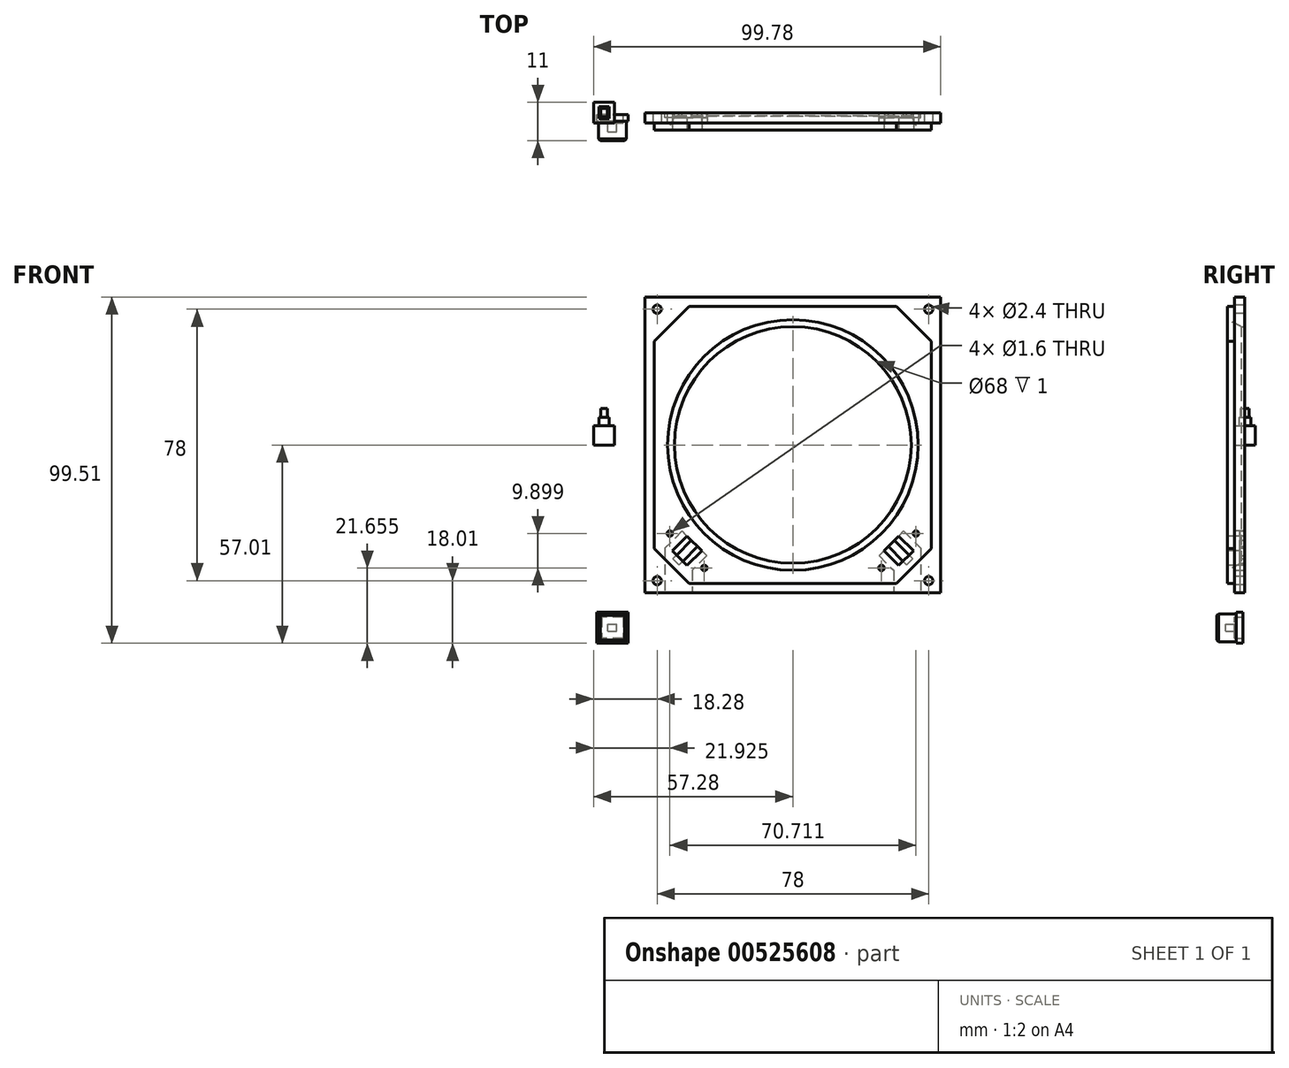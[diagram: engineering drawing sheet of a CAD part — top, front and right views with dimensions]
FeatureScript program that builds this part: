
annotation { "Feature Type Name" : "Feature", "Feature Type Description" : "" }
export const myFeature = defineFeature(function(context is Context, id is Id, definition is map)
    precondition{}
    {
        {
            var Q0;
            Q0=qCreatedBy(makeId("Front.planeOp"),FACE);
            cPlane(context, id + "F0", {"entities" : qUnion([Q0]), "cplaneType" : CPlaneType.OFFSET, "offset" : 3 * mm, "width" : 150 * mm, "height" : 150 * mm});
        }
        {
            var Q0;
            Q0=qCreatedBy(id+"F0.planeOp",FACE);
            var sketch = newSketch(context, id + "F1", { "sketchPlane" : qUnion([Q0])});
            skLineSegment(sketch, "E0.0", {"start": v(39.8, 29.8) * mm, "end": v(39.8, 0) * mm});
            skLineSegment(sketch, "E0.1", {"start": v(39.8, -29.8) * mm, "end": v(29.8, -39.8) * mm});
            skLineSegment(sketch, "E0.2", {"start": v(29.8, -39.8) * mm, "end": v(0, -39.8) * mm});
            skLineSegment(sketch, "E0.3", {"start": v(-29.8, -39.8) * mm, "end": v(-39.8, -29.8) * mm});
            skLineSegment(sketch, "E0.4", {"start": v(-39.8, -29.8) * mm, "end": v(-39.8, 0) * mm});
            skLineSegment(sketch, "E0.5", {"start": v(-39.8, 29.8) * mm, "end": v(-29.8, 39.8) * mm});
            skLineSegment(sketch, "E0.6", {"start": v(-29.8, 39.8) * mm, "end": v(0, 39.8) * mm});
            skLineSegment(sketch, "E0.7", {"start": v(29.8, 39.8) * mm, "end": v(39.8, 29.8) * mm});
            skPoint(sketch, "E1", {"position": v(0, 0) * mm});
            skLineSegment(sketch, "E2", {"start": v(0, 39.8) * mm, "end": v(29.8, 39.8) * mm});
            skLineSegment(sketch, "E3", {"start": v(-39.8, 0) * mm, "end": v(-39.8, 29.8) * mm});
            skLineSegment(sketch, "E4", {"start": v(39.8, 0) * mm, "end": v(39.8, -29.8) * mm});
            skLineSegment(sketch, "E5", {"start": v(0, -39.8) * mm, "end": v(-29.8, -39.8) * mm});
            skSolve(sketch);
        }
        {
            var Q0;
            Q0=qSketchRegion(id+"F1",true);
            extrude(context, id + "F2", {"entities" : qUnion([Q0]), "depth" : 2 * mm});
        }
        {
            var Q0;
            Q0=makeQuery(id+"F2.opExtrude","CAP_FACE",FACE,{"disambiguationData":[OSD([sQuery(id+"F1.wireOp",EDGE,"E0.0"),sQuery(id+"F1.wireOp",EDGE,"E0.1"),sQuery(id+"F1.wireOp",EDGE,"E0.2"),sQuery(id+"F1.wireOp",EDGE,"E0.3"),sQuery(id+"F1.wireOp",EDGE,"E0.4"),sQuery(id+"F1.wireOp",EDGE,"E0.5"),sQuery(id+"F1.wireOp",EDGE,"E0.6"),sQuery(id+"F1.wireOp",EDGE,"E0.7"),sQuery(id+"F1.wireOp",EDGE,"E2"),sQuery(id+"F1.wireOp",EDGE,"E3"),sQuery(id+"F1.wireOp",EDGE,"E4"),sQuery(id+"F1.wireOp",EDGE,"E5")])],"isStart":true});
            var sketch = newSketch(context, id + "F3", { "sketchPlane" : qUnion([Q0])});
            skLineSegment(sketch, "E6.bottom", {"start": v(-42.5, -42.5) * mm, "end": v(42.5, -42.5) * mm});
            skLineSegment(sketch, "E6.top", {"start": v(-42.5, 42.5) * mm, "end": v(42.5, 42.5) * mm});
            skLineSegment(sketch, "E6.left", {"start": v(-42.5, -42.5) * mm, "end": v(-42.5, 42.5) * mm});
            skLineSegment(sketch, "E6.right", {"start": v(42.5, -42.5) * mm, "end": v(42.5, 42.5) * mm});
            skPoint(sketch, "E6.middle", {"position": v(0, 0) * mm});
            skSolve(sketch);
        }
        {
            var Q0;
            Q0=qSketchRegion(id+"F3",true);
            extrude(context, id + "F4", {"entities" : qUnion([Q0]), "operationType" : NewBodyOperationType.ADD, "depth" : 3 * mm, "offsetDistance" : 25 * mm});
        }
        {
            var Q0;
            Q0=makeQuery(id+"F2.opExtrude","CAP_FACE",FACE,{"disambiguationData":[OSD([sQuery(id+"F1.wireOp",EDGE,"E0.0"),sQuery(id+"F1.wireOp",EDGE,"E0.1"),sQuery(id+"F1.wireOp",EDGE,"E0.2"),sQuery(id+"F1.wireOp",EDGE,"E0.3"),sQuery(id+"F1.wireOp",EDGE,"E0.4"),sQuery(id+"F1.wireOp",EDGE,"E0.5"),sQuery(id+"F1.wireOp",EDGE,"E0.6"),sQuery(id+"F1.wireOp",EDGE,"E0.7"),sQuery(id+"F1.wireOp",EDGE,"E2"),sQuery(id+"F1.wireOp",EDGE,"E3"),sQuery(id+"F1.wireOp",EDGE,"E4"),sQuery(id+"F1.wireOp",EDGE,"E5")])],"isStart":false});
            var sketch = newSketch(context, id + "F5", { "sketchPlane" : qUnion([Q0])});
            skCircle(sketch, "E7", {"center": v(0, 0) * mm, "radius": 38 * mm});
            skCircle(sketch, "E8", {"center": v(-39, 39) * mm, "radius": 1.5 * mm});
            skCircle(sketch, "E9", {"center": v(39, 39) * mm, "radius": 1.5 * mm});
            skCircle(sketch, "E10", {"center": v(-39, -39) * mm, "radius": 1.5 * mm});
            skCircle(sketch, "E11", {"center": v(39, -39) * mm, "radius": 1.5 * mm});
            skSolve(sketch);
        }
        {
            var Q0;
            Q0=sQuery(id+"F5.wireOp",VERTEX,"E8.center");
            var Q1;
            Q1=sQuery(id+"F5.wireOp",VERTEX,"E9.center");
            var Q2;
            Q2=sQuery(id+"F5.wireOp",VERTEX,"E11.center");
            var Q3;
            Q3=sQuery(id+"F5.wireOp",VERTEX,"E10.center");
            var Q4;
            Q4=makeQuery(id+"F2.opExtrude","SWEPT_BODY",BODY,{"disambiguationData":[OSD([sQuery(id+"F1.wireOp",EDGE,"E0.0"),sQuery(id+"F1.wireOp",EDGE,"E0.1"),sQuery(id+"F1.wireOp",EDGE,"E0.2"),sQuery(id+"F1.wireOp",EDGE,"E0.3"),sQuery(id+"F1.wireOp",EDGE,"E0.4"),sQuery(id+"F1.wireOp",EDGE,"E0.5"),sQuery(id+"F1.wireOp",EDGE,"E0.6"),sQuery(id+"F1.wireOp",EDGE,"E0.7"),sQuery(id+"F1.wireOp",EDGE,"E2"),sQuery(id+"F1.wireOp",EDGE,"E3"),sQuery(id+"F1.wireOp",EDGE,"E4"),sQuery(id+"F1.wireOp",EDGE,"E5")])]});
            hole(context, id + "F6", {"style" : HoleStyle.SIMPLE, "endStyle" : HoleEndStyle.THROUGH, "holeDiameter" : 2.4 * mm, "locations" : qUnion([Q0, Q1, Q2, Q3]), "scope" : qUnion([Q4]), "majorDiameter" : 5 * mm, "tappedDepth" : 12 * mm, "tapClearance" : 3});
        }
        {
            var Q0;
            Q0=sQuery(id+"F5.wireOp",VERTEX,"E7.center");
            var Q1;
            Q1=makeQuery(id+"F2.opExtrude","SWEPT_BODY",BODY,{"disambiguationData":[OSD([sQuery(id+"F1.wireOp",EDGE,"E0.0"),sQuery(id+"F1.wireOp",EDGE,"E0.1"),sQuery(id+"F1.wireOp",EDGE,"E0.2"),sQuery(id+"F1.wireOp",EDGE,"E0.3"),sQuery(id+"F1.wireOp",EDGE,"E0.4"),sQuery(id+"F1.wireOp",EDGE,"E0.5"),sQuery(id+"F1.wireOp",EDGE,"E0.6"),sQuery(id+"F1.wireOp",EDGE,"E0.7"),sQuery(id+"F1.wireOp",EDGE,"E2"),sQuery(id+"F1.wireOp",EDGE,"E3"),sQuery(id+"F1.wireOp",EDGE,"E4"),sQuery(id+"F1.wireOp",EDGE,"E5")])]});
            hole(context, id + "F7", {"style" : HoleStyle.SIMPLE, "endStyle" : HoleEndStyle.THROUGH, "holeDiameter" : 76 * mm, "locations" : qUnion([Q0]), "scope" : qUnion([Q1]), "majorDiameter" : 5 * mm, "tappedDepth" : 12 * mm, "tapClearance" : 3});
        }
        {
            var Q0;
            Q0=qCreatedBy(makeId("Right.planeOp"),FACE);
            var sketch = newSketch(context, id + "F8", { "sketchPlane" : qUnion([Q0])});
            skLineSegment(sketch, "E12", {"start": v(-5, 38) * mm, "end": v(-5, 36) * mm});
            skLineSegment(sketch, "E13", {"start": v(0, 34) * mm, "end": v(0, 38) * mm});
            skLineSegment(sketch, "E14", {"start": v(0, 38) * mm, "end": v(-5, 38) * mm});
            skLineSegment(sketch, "E15", {"start": v(0, 34) * mm, "end": v(-1, 34) * mm});
            skLineSegment(sketch, "E16", {"start": v(-1, 34) * mm, "end": v(-5, 36) * mm});
            skLineSegment(sketch, "E17", {"start": v(0, 0) * mm, "end": v(-24.42, 0) * mm, "construction": true});
            skSolve(sketch);
        }
        {
            var Q0;
            Q0 = qSketchRegion(id + "F8", true);
            var Q1;
            Q1=sQuery(id+"F8.wireOp",EDGE,"E17");
            revolve(context, id + "F9", {"operationType" : NewBodyOperationType.ADD, "entities" : qUnion([Q0]), "axis" : qUnion([Q1]), "revolveType" : RevolveType.FULL});
        }
        {
            var Q0;
            Q0=makeQuery(id+"F9.boolean.opBoolean","MERGE",FACE,{"derivedFrom":[makeQuery(id+"F2.opExtrude","CAP_FACE",FACE,{"disambiguationData":[OSD([sQuery(id+"F1.wireOp",EDGE,"E0.0"),sQuery(id+"F1.wireOp",EDGE,"E0.1"),sQuery(id+"F1.wireOp",EDGE,"E0.2"),sQuery(id+"F1.wireOp",EDGE,"E0.3"),sQuery(id+"F1.wireOp",EDGE,"E0.4"),sQuery(id+"F1.wireOp",EDGE,"E0.5"),sQuery(id+"F1.wireOp",EDGE,"E0.6"),sQuery(id+"F1.wireOp",EDGE,"E0.7"),sQuery(id+"F1.wireOp",EDGE,"E2"),sQuery(id+"F1.wireOp",EDGE,"E3"),sQuery(id+"F1.wireOp",EDGE,"E4"),sQuery(id+"F1.wireOp",EDGE,"E5")])],"isStart":false}),makeQuery(id+"F9.opRevolve","SWEPT_FACE",FACE,{"disambiguationData":[OSD([sQuery(id+"F8.wireOp",EDGE,"E12")])]})]});
            var sketch = newSketch(context, id + "F10", { "sketchPlane" : qUnion([Q0])});
            skLineSegment(sketch, "E18.bottom", {"start": v(-26.16, -30.4) * mm, "end": v(-30.4, -34.65) * mm});
            skLineSegment(sketch, "E18.top", {"start": v(-30.4, -26.16) * mm, "end": v(-34.65, -30.4) * mm});
            skLineSegment(sketch, "E18.left", {"start": v(-26.16, -30.4) * mm, "end": v(-30.4, -26.16) * mm});
            skLineSegment(sketch, "E18.right", {"start": v(-30.4, -34.65) * mm, "end": v(-34.65, -30.4) * mm});
            skPoint(sketch, "E18.middle", {"position": v(-30.4, -30.4) * mm});
            skLineSegment(sketch, "E19", {"start": v(0, 0) * mm, "end": v(-49.8, -49.8) * mm, "construction": true});
            skLineSegment(sketch, "E20", {"start": v(0, 0) * mm, "end": v(0, -7.55) * mm, "construction": true});
            skCircle(sketch, "E21", {"center": v(-35.36, -25.46) * mm, "radius": 0.8 * mm});
            skLineSegment(sketch, "E22", {"start": v(-30.4, -24.04) * mm, "end": v(-36.77, -30.4) * mm, "construction": true});
            skLineSegment(sketch, "E23", {"start": v(-36.77, -30.4) * mm, "end": v(-30.4, -36.77) * mm, "construction": true});
            skLineSegment(sketch, "E24", {"start": v(-30.4, -36.77) * mm, "end": v(-24.04, -30.4) * mm, "construction": true});
            skLineSegment(sketch, "E25", {"start": v(-24.04, -30.4) * mm, "end": v(-30.4, -24.04) * mm, "construction": true});
            skCircle(sketch, "E26", {"center": v(-25.46, -35.36) * mm, "radius": 0.8 * mm});
            skLineSegment(sketch, "E27.MirrorCS", {"start": v(0, 0) * mm, "end": v(49.8, -49.8) * mm, "construction": true});
            skCircle(sketch, "E28.MirrorC", {"center": v(25.46, -35.36) * mm, "radius": 0.8 * mm});
            skCircle(sketch, "E29.MirrorC", {"center": v(35.36, -25.46) * mm, "radius": 0.8 * mm});
            skPoint(sketch, "E30.MirrorP", {"position": v(30.4, -30.4) * mm});
            skLineSegment(sketch, "E31.MirrorCS", {"start": v(36.77, -30.4) * mm, "end": v(30.4, -36.77) * mm, "construction": true});
            skLineSegment(sketch, "E32.MirrorCS", {"start": v(24.04, -30.4) * mm, "end": v(30.4, -24.04) * mm, "construction": true});
            skLineSegment(sketch, "E33.MirrorCS", {"start": v(30.4, -24.04) * mm, "end": v(36.77, -30.4) * mm, "construction": true});
            skLineSegment(sketch, "E34.MirrorCS", {"start": v(30.4, -36.77) * mm, "end": v(24.04, -30.4) * mm, "construction": true});
            skLineSegment(sketch, "E35.MirrorCS", {"start": v(30.4, -34.65) * mm, "end": v(34.65, -30.4) * mm});
            skLineSegment(sketch, "E36.MirrorCS", {"start": v(30.4, -26.16) * mm, "end": v(34.65, -30.4) * mm});
            skLineSegment(sketch, "E37.MirrorCS", {"start": v(26.16, -30.4) * mm, "end": v(30.4, -34.65) * mm});
            skLineSegment(sketch, "E38.MirrorCS", {"start": v(26.16, -30.4) * mm, "end": v(30.4, -26.16) * mm});
            skSolve(sketch);
        }
        {
            var Q0;
            Q0 = qSketchRegion(id + "F10", true);
            extrude(context, id + "F11", {"entities" : qUnion([Q0]), "operationType" : NewBodyOperationType.REMOVE, "oppositeDirection" : true, "depth" : 5 * mm, "offsetDistance" : 25 * mm});
        }
        {
            var Q0;
            Q0=makeQuery(id+"F9.boolean.opBoolean","MERGE",FACE,{"derivedFrom":[makeQuery(id+"F4.opExtrude","CAP_FACE",FACE,{"disambiguationData":[OSD([sQuery(id+"F3.wireOp",EDGE,"E6.bottom"),sQuery(id+"F3.wireOp",EDGE,"E6.top"),sQuery(id+"F3.wireOp",EDGE,"E6.left"),sQuery(id+"F3.wireOp",EDGE,"E6.right")])],"isStart":false}),makeQuery(id+"F9.opRevolve","SWEPT_FACE",FACE,{"disambiguationData":[OSD([sQuery(id+"F8.wireOp",EDGE,"E13")])]})]});
            var sketch = newSketch(context, id + "F12", { "sketchPlane" : qUnion([Q0])});
            skLineSegment(sketch, "E39.bottom", {"start": v(31.64, -33.41) * mm, "end": v(27.4, -29.17) * mm});
            skLineSegment(sketch, "E39.top", {"start": v(33.41, -31.64) * mm, "end": v(29.17, -27.4) * mm});
            skLineSegment(sketch, "E39.left", {"start": v(33.41, -31.64) * mm, "end": v(31.64, -33.41) * mm});
            skLineSegment(sketch, "E39.right", {"start": v(29.17, -27.4) * mm, "end": v(27.4, -29.17) * mm});
            skPoint(sketch, "E39.middle", {"position": v(30.4, -30.4) * mm});
            skLineSegment(sketch, "E40", {"start": v(0, 0) * mm, "end": v(0, -24.07) * mm, "construction": true});
            skLineSegment(sketch, "E41.MirrorCS", {"start": v(-29.17, -27.4) * mm, "end": v(-27.4, -29.17) * mm});
            skLineSegment(sketch, "E42.MirrorCS", {"start": v(-33.41, -31.64) * mm, "end": v(-31.64, -33.41) * mm});
            skLineSegment(sketch, "E43.MirrorCS", {"start": v(-31.64, -33.41) * mm, "end": v(-27.4, -29.17) * mm});
            skLineSegment(sketch, "E44.MirrorCS", {"start": v(-33.41, -31.64) * mm, "end": v(-29.17, -27.4) * mm});
            skPoint(sketch, "E45.MirrorP", {"position": v(-30.4, -30.4) * mm});
            skSolve(sketch);
        }
        {
            var Q0;
            Q0 = qSketchRegion(id + "F12", true);
            extrude(context, id + "F13", {"entities" : qUnion([Q0]), "operationType" : NewBodyOperationType.ADD, "oppositeDirection" : true, "depth" : 1.5 * mm, "offsetDistance" : 25 * mm});
        }
        {
            var Q0;
            Q0=qCreatedBy(makeId("Front.planeOp"),FACE);
            var sketch = newSketch(context, id + "F14", { "sketchPlane" : qUnion([Q0])});
            skLineSegment(sketch, "E46.bottom", {"start": v(-47.88, -56.51) * mm, "end": v(-55.88, -56.51) * mm});
            skLineSegment(sketch, "E46.top", {"start": v(-47.88, -48.51) * mm, "end": v(-55.88, -48.51) * mm});
            skLineSegment(sketch, "E46.left", {"start": v(-47.88, -56.51) * mm, "end": v(-47.88, -48.51) * mm});
            skLineSegment(sketch, "E46.right", {"start": v(-55.88, -56.51) * mm, "end": v(-55.88, -48.51) * mm});
            skPoint(sketch, "E46.middle", {"position": v(-51.88, -52.51) * mm});
            skSolve(sketch);
        }
        {
            var Q0;
            Q0 = qSketchRegion(id + "F14", true);
            extrude(context, id + "F15", {"entities" : qUnion([Q0]), "depth" : 8 * mm, "offsetDistance" : 25 * mm});
        }
        {
            var Q0;
            Q0=makeQuery(id+"F15.opExtrude","CAP_FACE",FACE,{"disambiguationData":[OSD([sQuery(id+"F14.wireOp",EDGE,"E46.bottom"),sQuery(id+"F14.wireOp",EDGE,"E46.top"),sQuery(id+"F14.wireOp",EDGE,"E46.left"),sQuery(id+"F14.wireOp",EDGE,"E46.right")])],"isStart":true});
            var sketch = newSketch(context, id + "F16", { "sketchPlane" : qUnion([Q0])});
            skLineSegment(sketch, "E47.bottom", {"start": v(54.98, -55.61) * mm, "end": v(48.78, -55.61) * mm});
            skLineSegment(sketch, "E47.top", {"start": v(54.98, -49.41) * mm, "end": v(48.78, -49.41) * mm});
            skLineSegment(sketch, "E47.left", {"start": v(54.98, -55.61) * mm, "end": v(54.98, -49.41) * mm});
            skLineSegment(sketch, "E47.right", {"start": v(48.78, -55.61) * mm, "end": v(48.78, -49.41) * mm});
            skPoint(sketch, "E47.middle", {"position": v(51.88, -52.51) * mm});
            skSolve(sketch);
        }
        {
            var Q0;
            Q0 = qSketchRegion(id + "F16", true);
            extrude(context, id + "F17", {"entities" : qUnion([Q0]), "operationType" : NewBodyOperationType.REMOVE, "oppositeDirection" : true, "depth" : 3 * mm, "offsetDistance" : 25 * mm});
        }
        {
            var Q0;
            Q0=makeQuery(id+"F17.boolean.opBoolean","COPY",FACE,{"derivedFrom":makeQuery(id+"F17.opExtrude","CAP_FACE",FACE,{"disambiguationData":[OSD([sQuery(id+"F16.wireOp",EDGE,"E47.bottom"),sQuery(id+"F16.wireOp",EDGE,"E47.top"),sQuery(id+"F16.wireOp",EDGE,"E47.left"),sQuery(id+"F16.wireOp",EDGE,"E47.right")])],"isStart":false})});
            var sketch = newSketch(context, id + "F18", { "sketchPlane" : qUnion([Q0])});
            skLineSegment(sketch, "E48.bottom", {"start": v(53.13, -53.51) * mm, "end": v(50.63, -53.51) * mm});
            skLineSegment(sketch, "E48.top", {"start": v(53.13, -51.51) * mm, "end": v(50.63, -51.51) * mm});
            skLineSegment(sketch, "E48.left", {"start": v(53.13, -53.51) * mm, "end": v(53.13, -51.51) * mm});
            skLineSegment(sketch, "E48.right", {"start": v(50.63, -53.51) * mm, "end": v(50.63, -51.51) * mm});
            skPoint(sketch, "E48.middle", {"position": v(51.88, -52.51) * mm});
            skSolve(sketch);
        }
        {
            var Q0;
            Q0 = qSketchRegion(id + "F18", true);
            extrude(context, id + "F19", {"entities" : qUnion([Q0]), "operationType" : NewBodyOperationType.REMOVE, "oppositeDirection" : true, "depth" : 2.5 * mm, "offsetDistance" : 25 * mm});
        }
        {
            var Q0;
            Q0=makeQuery(id+"F15.opExtrude","CAP_FACE",FACE,{"disambiguationData":[OSD([sQuery(id+"F14.wireOp",EDGE,"E46.bottom"),sQuery(id+"F14.wireOp",EDGE,"E46.top"),sQuery(id+"F14.wireOp",EDGE,"E46.left"),sQuery(id+"F14.wireOp",EDGE,"E46.right")])],"isStart":true});
            var sketch = newSketch(context, id + "F20", { "sketchPlane" : qUnion([Q0])});
            skLineSegment(sketch, "E49.bottom", {"start": v(47.38, -57.01) * mm, "end": v(56.38, -57.01) * mm});
            skLineSegment(sketch, "E49.top", {"start": v(47.38, -48.01) * mm, "end": v(56.38, -48.01) * mm});
            skLineSegment(sketch, "E49.left", {"start": v(47.38, -57.01) * mm, "end": v(47.38, -48.01) * mm});
            skLineSegment(sketch, "E49.right", {"start": v(56.38, -57.01) * mm, "end": v(56.38, -48.01) * mm});
            skPoint(sketch, "E49.middle", {"position": v(51.88, -52.51) * mm});
            skPoint(sketch, "E49.middle.positionSnap0", {"position": v(51.88, -49.41) * mm});
            skPoint(sketch, "E49.middle.positionSnap1", {"position": v(54.98, -52.51) * mm});
            skPoint(sketch, "E49.centerSnap0", {"position": v(51.88, -49.41) * mm});
            skPoint(sketch, "E49.centerSnap1", {"position": v(54.98, -52.51) * mm});
            skLineSegment(sketch, "E50.bottom", {"start": v(55.88, -48.51) * mm, "end": v(47.88, -48.51) * mm});
            skLineSegment(sketch, "E50.top", {"start": v(55.88, -56.51) * mm, "end": v(47.88, -56.51) * mm});
            skLineSegment(sketch, "E50.left", {"start": v(55.88, -48.51) * mm, "end": v(55.88, -56.51) * mm});
            skLineSegment(sketch, "E50.right", {"start": v(47.88, -48.51) * mm, "end": v(47.88, -56.51) * mm});
            skSolve(sketch);
        }
        {
            var Q0;
            Q0 = qSketchRegion(id + "F20", true);
            extrude(context, id + "F21", {"entities" : qUnion([Q0]), "operationType" : NewBodyOperationType.ADD, "oppositeDirection" : true, "depth" : 2.5 * mm, "offsetDistance" : 25 * mm});
        }
        {
            var Q0;
            Q0=makeQuery(id+"F13.boolean.opBoolean","MERGE",FACE,{"derivedFrom":[makeQuery(id+"F9.boolean.opBoolean","MERGE",FACE,{"derivedFrom":[makeQuery(id+"F4.opExtrude","CAP_FACE",FACE,{"disambiguationData":[OSD([sQuery(id+"F3.wireOp",EDGE,"E6.bottom"),sQuery(id+"F3.wireOp",EDGE,"E6.top"),sQuery(id+"F3.wireOp",EDGE,"E6.left"),sQuery(id+"F3.wireOp",EDGE,"E6.right")])],"isStart":false}),makeQuery(id+"F9.opRevolve","SWEPT_FACE",FACE,{"disambiguationData":[OSD([sQuery(id+"F8.wireOp",EDGE,"E13")])]})]}),makeQuery(id+"F13.opExtrude","CAP_FACE",FACE,{"disambiguationData":[OSD([sQuery(id+"F12.wireOp",EDGE,"E39.bottom"),sQuery(id+"F12.wireOp",EDGE,"E39.top"),sQuery(id+"F12.wireOp",EDGE,"E39.left"),sQuery(id+"F12.wireOp",EDGE,"E39.right")])],"isStart":true})]});
            var sketch = newSketch(context, id + "F22", { "sketchPlane" : qUnion([Q0])});
            skLineSegment(sketch, "E51", {"start": v(30.4, -34.65) * mm, "end": v(31.64, -33.41) * mm});
            skLineSegment(sketch, "E52", {"start": v(31.64, -33.41) * mm, "end": v(32.7, -34.47) * mm});
            skLineSegment(sketch, "E53", {"start": v(33.41, -31.64) * mm, "end": v(34.47, -32.7) * mm});
            skLineSegment(sketch, "E54", {"start": v(34.47, -32.7) * mm, "end": v(32.7, -34.47) * mm});
            skLineSegment(sketch, "E55", {"start": v(33.41, -31.64) * mm, "end": v(34.65, -30.4) * mm});
            skLineSegment(sketch, "E56", {"start": v(26.16, -30.4) * mm, "end": v(24.75, -31.82) * mm});
            skLineSegment(sketch, "E57", {"start": v(24.75, -31.82) * mm, "end": v(29, -36.06) * mm});
            skLineSegment(sketch, "E58", {"start": v(29, -36.06) * mm, "end": v(29, -42.5) * mm});
            skLineSegment(sketch, "E59", {"start": v(26.16, -30.4) * mm, "end": v(30.4, -34.65) * mm});
            skLineSegment(sketch, "E60", {"start": v(30.4, -26.16) * mm, "end": v(31.82, -24.75) * mm});
            skLineSegment(sketch, "E61", {"start": v(31.82, -24.75) * mm, "end": v(36.77, -29.7) * mm});
            skLineSegment(sketch, "E62", {"start": v(30.4, -26.16) * mm, "end": v(34.65, -30.4) * mm});
            skLineSegment(sketch, "E63", {"start": v(36.77, -29.7) * mm, "end": v(36.77, -42.5) * mm});
            skLineSegment(sketch, "E64", {"start": v(36.77, -42.5) * mm, "end": v(29, -42.5) * mm});
            skLineSegment(sketch, "E65", {"start": v(0, 0) * mm, "end": v(0, -22.57) * mm, "construction": true});
            skLineSegment(sketch, "E66.MirrorCS", {"start": v(-30.4, -34.65) * mm, "end": v(-31.64, -33.41) * mm});
            skLineSegment(sketch, "E67.MirrorCS", {"start": v(-31.64, -33.41) * mm, "end": v(-32.7, -34.47) * mm});
            skLineSegment(sketch, "E68.MirrorCS", {"start": v(-34.47, -32.7) * mm, "end": v(-32.7, -34.47) * mm});
            skLineSegment(sketch, "E69.MirrorCS", {"start": v(-33.41, -31.64) * mm, "end": v(-34.65, -30.4) * mm});
            skLineSegment(sketch, "E70.MirrorCS", {"start": v(-33.41, -31.64) * mm, "end": v(-34.47, -32.7) * mm});
            skLineSegment(sketch, "E71.MirrorCS", {"start": v(-26.16, -30.4) * mm, "end": v(-24.75, -31.82) * mm});
            skLineSegment(sketch, "E72.MirrorCS", {"start": v(-30.4, -26.16) * mm, "end": v(-31.82, -24.75) * mm});
            skLineSegment(sketch, "E73.MirrorCS", {"start": v(-24.75, -31.82) * mm, "end": v(-29, -36.06) * mm});
            skLineSegment(sketch, "E74.MirrorCS", {"start": v(-36.77, -42.5) * mm, "end": v(-29, -42.5) * mm});
            skLineSegment(sketch, "E75.MirrorCS", {"start": v(-29, -36.06) * mm, "end": v(-29, -42.5) * mm});
            skLineSegment(sketch, "E76.MirrorCS", {"start": v(-36.77, -29.7) * mm, "end": v(-36.77, -42.5) * mm});
            skLineSegment(sketch, "E77.MirrorCS", {"start": v(-30.4, -26.16) * mm, "end": v(-34.65, -30.4) * mm});
            skLineSegment(sketch, "E78.MirrorCS", {"start": v(-26.16, -30.4) * mm, "end": v(-30.4, -34.65) * mm});
            skLineSegment(sketch, "E79.MirrorCS", {"start": v(-31.82, -24.75) * mm, "end": v(-36.77, -29.7) * mm});
            skSolve(sketch);
        }
        {
            var Q0;
            Q0 = qSketchRegion(id + "F22", true);
            extrude(context, id + "F23", {"entities" : qUnion([Q0]), "operationType" : NewBodyOperationType.REMOVE, "oppositeDirection" : true, "depth" : 1.5 * mm, "offsetDistance" : 25 * mm});
        }
        {
            var Q0;
            Q0=qCreatedBy(makeId("Top.planeOp"),FACE);
            var sketch = newSketch(context, id + "F24", { "sketchPlane" : qUnion([Q0])});
            skLineSegment(sketch, "E80.bottom", {"start": v(-51.28, -3) * mm, "end": v(-57.28, -3) * mm});
            skLineSegment(sketch, "E80.top", {"start": v(-51.28, 3) * mm, "end": v(-57.28, 3) * mm});
            skLineSegment(sketch, "E80.left", {"start": v(-51.28, -3) * mm, "end": v(-51.28, 3) * mm});
            skLineSegment(sketch, "E80.right", {"start": v(-57.28, -3) * mm, "end": v(-57.28, 3) * mm});
            skPoint(sketch, "E80.middle", {"position": v(-54.28, 0) * mm});
            skSolve(sketch);
        }
        {
            var Q0;
            Q0 = qSketchRegion(id + "F24", true);
            extrude(context, id + "F25", {"entities" : qUnion([Q0]), "depth" : 5.5 * mm, "offsetDistance" : 25 * mm});
        }
        {
            var Q0;
            Q0=makeQuery(id+"F25.opExtrude","CAP_FACE",FACE,{"disambiguationData":[OSD([sQuery(id+"F24.wireOp",EDGE,"E80.bottom"),sQuery(id+"F24.wireOp",EDGE,"E80.top"),sQuery(id+"F24.wireOp",EDGE,"E80.left"),sQuery(id+"F24.wireOp",EDGE,"E80.right")])],"isStart":false});
            var sketch = newSketch(context, id + "F26", { "sketchPlane" : qUnion([Q0])});
            skLineSegment(sketch, "E81.bottom", {"start": v(-52.78, -1.75) * mm, "end": v(-55.78, -1.75) * mm});
            skLineSegment(sketch, "E81.top", {"start": v(-52.78, 1.75) * mm, "end": v(-55.78, 1.75) * mm});
            skLineSegment(sketch, "E81.left", {"start": v(-52.78, -1.75) * mm, "end": v(-52.78, 1.75) * mm});
            skLineSegment(sketch, "E81.right", {"start": v(-55.78, -1.75) * mm, "end": v(-55.78, 1.75) * mm});
            skPoint(sketch, "E81.middle", {"position": v(-54.28, 0) * mm});
            skPoint(sketch, "E81.middle.positionSnap0", {"position": v(-57.28, 0) * mm});
            skPoint(sketch, "E81.middle.positionSnap1", {"position": v(-54.28, 3) * mm});
            skPoint(sketch, "E81.centerSnap0", {"position": v(-57.28, 0) * mm});
            skPoint(sketch, "E81.centerSnap1", {"position": v(-54.28, 3) * mm});
            skSolve(sketch);
        }
        {
            var Q0;
            Q0 = qSketchRegion(id + "F26", true);
            extrude(context, id + "F27", {"entities" : qUnion([Q0]), "operationType" : NewBodyOperationType.ADD, "depth" : 2.5 * mm, "offsetDistance" : 25 * mm});
        }
        {
            var Q0;
            Q0=makeQuery(id+"F27.opExtrude","CAP_FACE",FACE,{"disambiguationData":[OSD([sQuery(id+"F26.wireOp",EDGE,"E81.bottom"),sQuery(id+"F26.wireOp",EDGE,"E81.top"),sQuery(id+"F26.wireOp",EDGE,"E81.left"),sQuery(id+"F26.wireOp",EDGE,"E81.right")])],"isStart":false});
            var sketch = newSketch(context, id + "F28", { "sketchPlane" : qUnion([Q0])});
            skLineSegment(sketch, "E82.bottom", {"start": v(-53.28, -1.25) * mm, "end": v(-55.28, -1.25) * mm});
            skLineSegment(sketch, "E82.top", {"start": v(-53.28, 1.25) * mm, "end": v(-55.28, 1.25) * mm});
            skLineSegment(sketch, "E82.left", {"start": v(-53.28, -1.25) * mm, "end": v(-53.28, 1.25) * mm});
            skLineSegment(sketch, "E82.right", {"start": v(-55.28, -1.25) * mm, "end": v(-55.28, 1.25) * mm});
            skPoint(sketch, "E82.middle", {"position": v(-54.28, 0) * mm});
            skPoint(sketch, "E82.middle.positionSnap0", {"position": v(-55.78, 0) * mm});
            skPoint(sketch, "E82.middle.positionSnap1", {"position": v(-54.28, 1.75) * mm});
            skPoint(sketch, "E82.centerSnap0", {"position": v(-55.78, 0) * mm});
            skPoint(sketch, "E82.centerSnap1", {"position": v(-54.28, 1.75) * mm});
            skSolve(sketch);
        }
        {
            var Q0;
            Q0 = qSketchRegion(id + "F28", true);
            extrude(context, id + "F29", {"entities" : qUnion([Q0]), "operationType" : NewBodyOperationType.ADD, "depth" : 2.5 * mm, "offsetDistance" : 25 * mm});
        }
        {
            var Q0;
            Q0=makeQuery(id+"F15.opExtrude","CAP_FACE",FACE,{"disambiguationData":[OSD([sQuery(id+"F14.wireOp",EDGE,"E46.bottom"),sQuery(id+"F14.wireOp",EDGE,"E46.top"),sQuery(id+"F14.wireOp",EDGE,"E46.left"),sQuery(id+"F14.wireOp",EDGE,"E46.right")])],"isStart":false});
            chamfer(context, id + "F30", {"entities" : qUnion([Q0]), "width" : 0.5 * mm, "tangentPropagation" : true});
        }
        {
            var Q0;
            Q0=makeQuery(id+"F21.opExtrude","SWEPT_FACE",FACE,{"disambiguationData":[OSD([sQuery(id+"F20.wireOp",EDGE,"E49.bottom")])]});
            var sketch = newSketch(context, id + "F31", { "sketchPlane" : qUnion([Q0])});
            skLineSegment(sketch, "E83.bottom", {"start": v(-56.38, 0) * mm, "end": v(-47.38, 0) * mm});
            skLineSegment(sketch, "E83.top", {"start": v(-56.38, 0.5) * mm, "end": v(-47.38, 0.5) * mm});
            skLineSegment(sketch, "E83.left", {"start": v(-56.38, 0) * mm, "end": v(-56.38, 0.5) * mm});
            skLineSegment(sketch, "E83.right", {"start": v(-47.38, 0) * mm, "end": v(-47.38, 0.5) * mm});
            skSolve(sketch);
        }
        {
            var Q0;
            Q0 = qSketchRegion(id + "F31", true);
            extrude(context, id + "F32", {"entities" : qUnion([Q0]), "operationType" : NewBodyOperationType.REMOVE, "oppositeDirection" : true, "depth" : 25 * mm, "offsetDistance" : 25 * mm});
        }
    });
